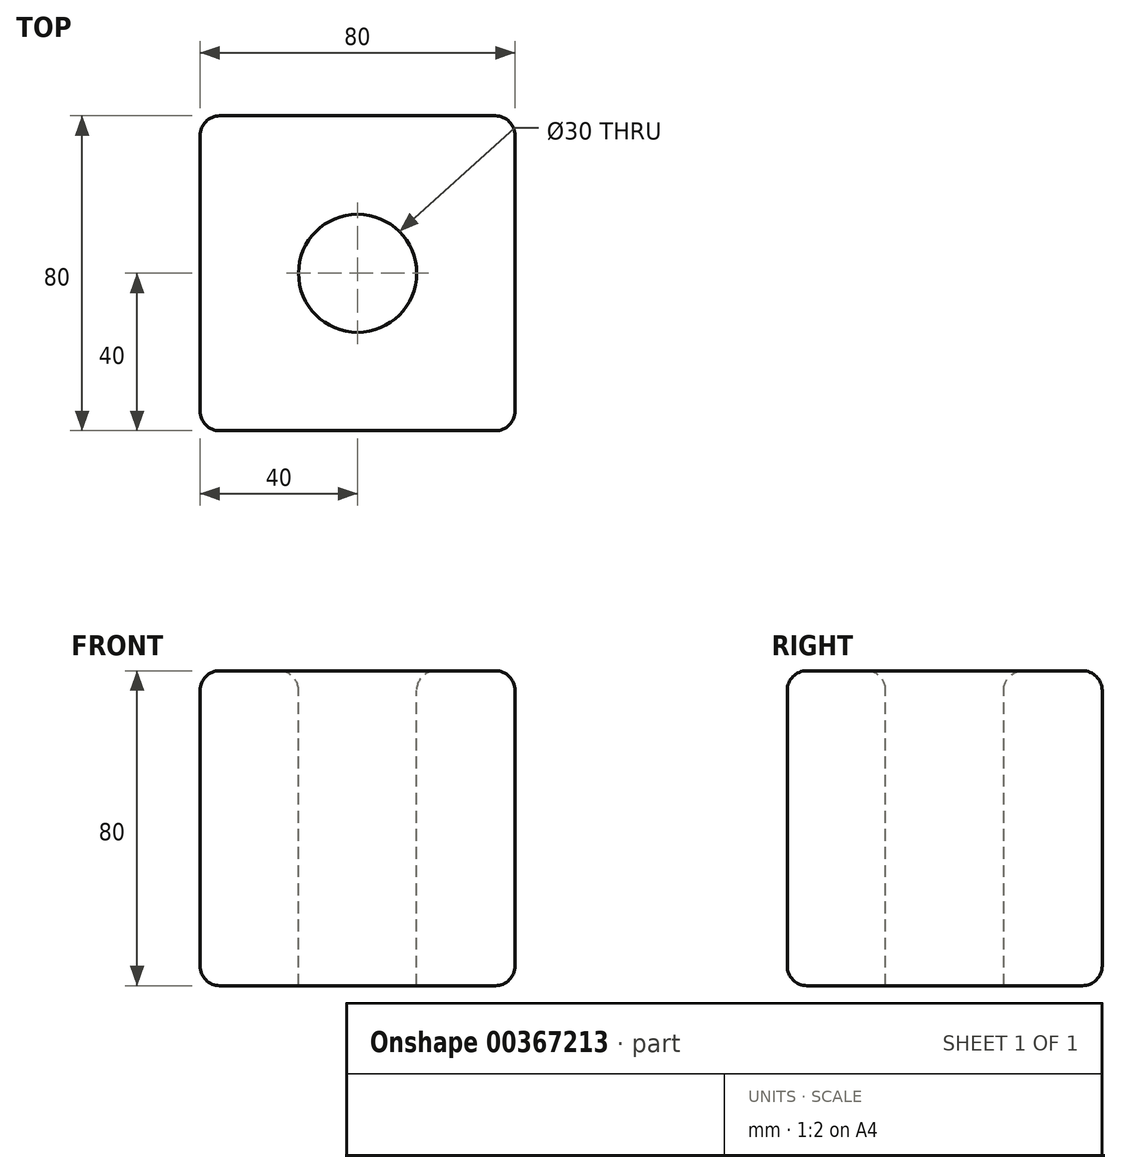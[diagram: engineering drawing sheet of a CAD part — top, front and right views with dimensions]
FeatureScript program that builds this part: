
annotation { "Feature Type Name" : "Feature", "Feature Type Description" : "" }
export const myFeature = defineFeature(function(context is Context, id is Id, definition is map)
    precondition{}
    {
        {
            var Q0;
            Q0=qCreatedBy(makeId("Top.planeOp"),FACE);
            var sketch = newSketch(context, id + "F0", { "sketchPlane" : qUnion([Q0])});
            skLineSegment(sketch, "E0.bottom", {"start": v(40, -40) * mm, "end": v(-40, -40) * mm});
            skLineSegment(sketch, "E0.top", {"start": v(40, 40) * mm, "end": v(-40, 40) * mm});
            skLineSegment(sketch, "E0.left", {"start": v(40, -40) * mm, "end": v(40, 40) * mm});
            skLineSegment(sketch, "E0.right", {"start": v(-40, -40) * mm, "end": v(-40, 40) * mm});
            skPoint(sketch, "E0.middle", {"position": v(0, 0) * mm});
            skSolve(sketch);
        }
        {
            var Q0;
            Q0=makeQuery(id+"F0.imprint","IMPRINT",FACE,{"disambiguationData":[TD([[makeQuery(id+"F0.imprint","IMPRINT",EDGE,{"derivedFrom":sQuery(id+"F0.wireOp",EDGE,"E0.bottom")}),-1.0]])]});
            extrude(context, id + "F1", {"entities" : qUnion([Q0]), "depth" : 80 * mm});
        }
        {
            var Q0;
            Q0=makeQuery(id+"F1.opExtrude","CAP_FACE",FACE,{"disambiguationData":[OSD([sQuery(id+"F0.wireOp",EDGE,"E0.bottom"),sQuery(id+"F0.wireOp",EDGE,"E0.top"),sQuery(id+"F0.wireOp",EDGE,"E0.left"),sQuery(id+"F0.wireOp",EDGE,"E0.right")])],"isStart":false});
            var sketch = newSketch(context, id + "F2", { "sketchPlane" : qUnion([Q0])});
            skCircle(sketch, "E1", {"center": v(0, 0) * mm, "radius": 15 * mm});
            skSolve(sketch);
        }
        {
            var Q0;
            Q0=makeQuery(id+"F2.imprint","IMPRINT",FACE,{"disambiguationData":[TD([[makeQuery(id+"F2.imprint","IMPRINT",EDGE,{"derivedFrom":sQuery(id+"F2.wireOp",EDGE,"E1")}),1.0]])]});
            extrude(context, id + "F3", {"entities" : qUnion([Q0]), "operationType" : NewBodyOperationType.REMOVE, "endBound" : BoundingType.THROUGH_ALL, "oppositeDirection" : true, "depth" : 25 * mm});
        }
        {
            var Q0;
            Q0=makeQuery(id+"F1.opExtrude","SWEPT_EDGE",EDGE,{"disambiguationData":[OSD([sQuery(id+"F0.wireOp",EDGE,"E0.bottom"),sQuery(id+"F0.wireOp",EDGE,"E0.right")])]});
            var Q1;
            Q1=makeQuery(id+"F1.opExtrude","CAP_EDGE",EDGE,{"disambiguationData":[OSD([sQuery(id+"F0.wireOp",EDGE,"E0.top")])],"isStart":false});
            var Q2;
            Q2=makeQuery(id+"F1.opExtrude","CAP_EDGE",EDGE,{"disambiguationData":[OSD([sQuery(id+"F0.wireOp",EDGE,"E0.bottom")])],"isStart":false});
            var Q3;
            Q3=makeQuery(id+"F1.opExtrude","CAP_EDGE",EDGE,{"disambiguationData":[OSD([sQuery(id+"F0.wireOp",EDGE,"E0.right")])],"isStart":false});
            var Q4;
            Q4=makeQuery(id+"F1.opExtrude","CAP_EDGE",EDGE,{"disambiguationData":[OSD([sQuery(id+"F0.wireOp",EDGE,"E0.left")])],"isStart":false});
            var Q5;
            Q5=makeQuery(id+"F1.opExtrude","CAP_FACE",FACE,{"disambiguationData":[OSD([sQuery(id+"F0.wireOp",EDGE,"E0.bottom"),sQuery(id+"F0.wireOp",EDGE,"E0.top"),sQuery(id+"F0.wireOp",EDGE,"E0.left"),sQuery(id+"F0.wireOp",EDGE,"E0.right")])],"isStart":false});
            var Q6;
            Q6=makeQuery(id+"F1.opExtrude","CAP_EDGE",EDGE,{"disambiguationData":[OSD([sQuery(id+"F0.wireOp",EDGE,"E0.right")])],"isStart":true});
            var Q7;
            Q7=makeQuery(id+"F1.opExtrude","SWEPT_EDGE",EDGE,{"disambiguationData":[OSD([sQuery(id+"F0.wireOp",EDGE,"E0.top"),sQuery(id+"F0.wireOp",EDGE,"E0.right")])]});
            var Q8;
            Q8=makeQuery(id+"F1.opExtrude","CAP_EDGE",EDGE,{"disambiguationData":[OSD([sQuery(id+"F0.wireOp",EDGE,"E0.left")])],"isStart":true});
            var Q9;
            Q9=makeQuery(id+"F1.opExtrude","SWEPT_EDGE",EDGE,{"disambiguationData":[OSD([sQuery(id+"F0.wireOp",EDGE,"E0.top"),sQuery(id+"F0.wireOp",EDGE,"E0.left")])]});
            var Q10;
            Q10=makeQuery(id+"F1.opExtrude","SWEPT_EDGE",EDGE,{"disambiguationData":[OSD([sQuery(id+"F0.wireOp",EDGE,"E0.bottom"),sQuery(id+"F0.wireOp",EDGE,"E0.left")])]});
            var Q11;
            Q11=makeQuery(id+"F1.opExtrude","SWEPT_FACE",FACE,{"disambiguationData":[OSD([sQuery(id+"F0.wireOp",EDGE,"E0.top")])]});
            var Q12;
            Q12=makeQuery(id+"F1.opExtrude","CAP_EDGE",EDGE,{"disambiguationData":[OSD([sQuery(id+"F0.wireOp",EDGE,"E0.bottom")])],"isStart":true});
            fillet(context, id + "F4", {"entities" : qUnion([Q0, Q1, Q2, Q3, Q4, Q5, Q6, Q7, Q8, Q9, Q10, Q11, Q12]), "radius" : 5 * mm, "tangentPropagation" : true, "allowEdgeOverflow" : false});
        }
    });
